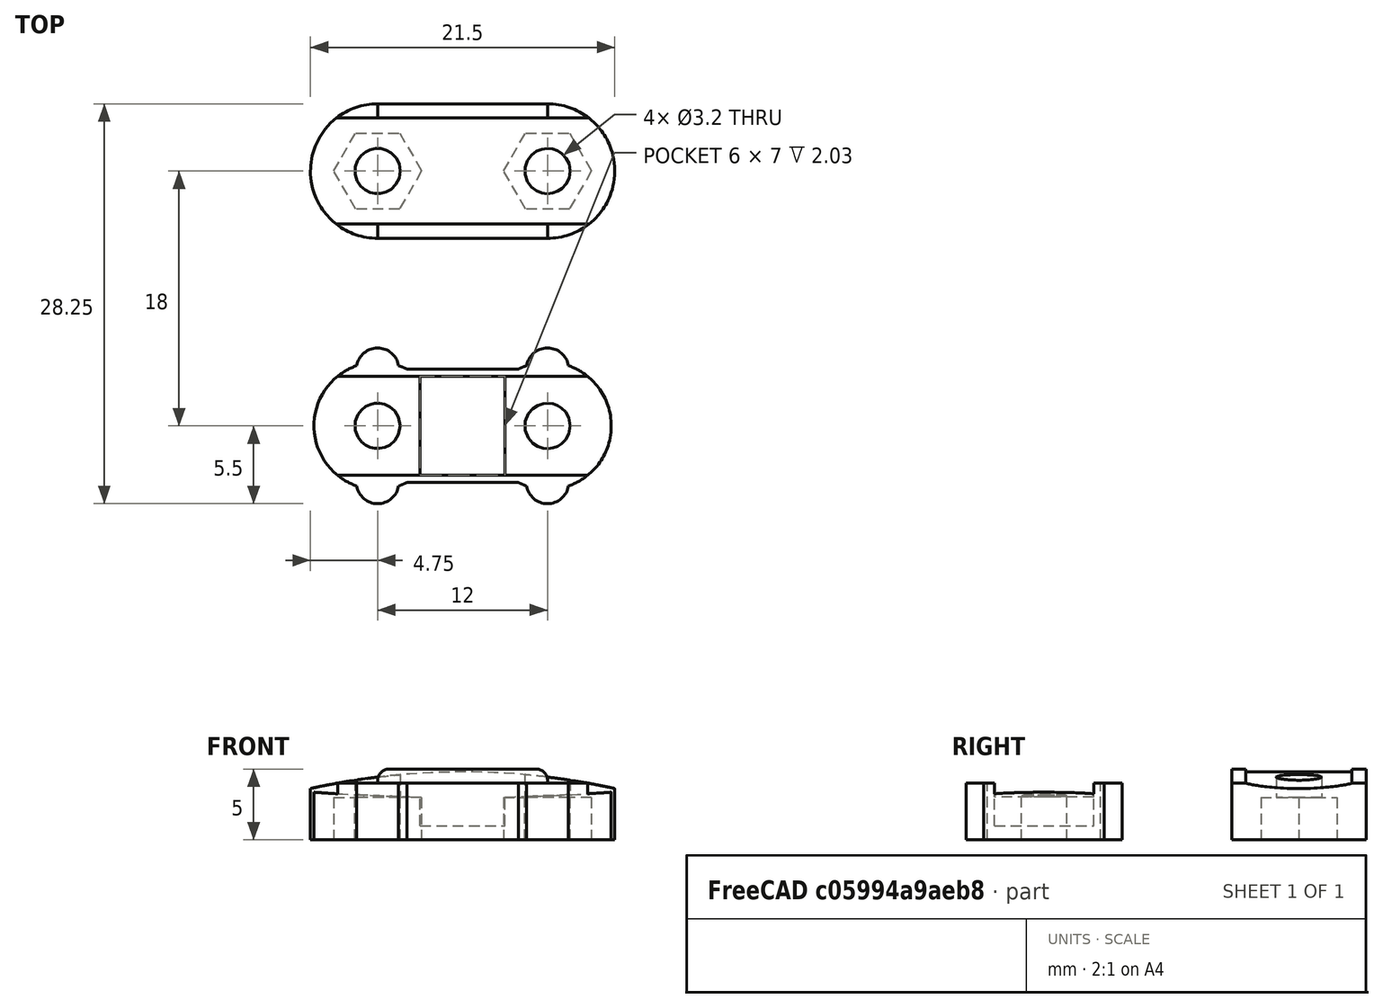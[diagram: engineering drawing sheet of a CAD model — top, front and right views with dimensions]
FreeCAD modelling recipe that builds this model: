
FCSTD DOCUMENT  (FreeCAD 0.16R4864 (Git))
Label: leafspring-mount
License: CC-BY 3.0
LicenseURL: http://creativecommons.org/licenses/by/3.0/
objects: Part::Cylinder×16, Part::Box×14, Part::Cut×12, Part::MultiFuse×10, Part::Extrusion×2, Part::RegularPolygon×1, Part::Feature×1, Part::Fillet×1
note: 57 computed .brp shape members not serialized (recipe doc carries the construction recipe); baked Part::Feature solids carry a one-line shape summary decoded from their .brp

FEATURE [Part::RegularPolygon] RegularPolygon  label="Regular polygon"
  Circumradius = 3.1
  Polygon = 6
FEATURE [Part::Cylinder] Cylinder
  Angle = 360
  Height = 4
  Radius = 4.5
FEATURE [Part::Cylinder] Cylinder001
  Angle = 360
  Height = 4
  Placement = pos=(12,0,0) rot=(0,0,1;0rad)
  Radius = 4.5
FEATURE [Part::Box] Box
  Height = 1
  Length = 12
  Placement = pos=(0,-4,0) rot=(0,0,1;0rad)
  Width = 8
FEATURE [Part::MultiFuse] Fusion
  Shapes = -> [Box,Cylinder001,Cylinder]
FEATURE [Part::Box] Box001
  Height = 4
  Length = 12
  Placement = pos=(0,-4,0) rot=(0,0,1;0rad)
  Width = 1
FEATURE [Part::Box] Box002
  Height = 4
  Length = 12
  Placement = pos=(0,3,0) rot=(0,0,1;0rad)
  Width = 1
FEATURE [Part::Box] Box003
  Height = 1
  Length = 12
  Placement = pos=(0,3.5,3) rot=(0,0,1;0rad)
  Width = 0.5
FEATURE [Part::MultiFuse] Fusion001
  Shapes = -> [Fusion,Box002,Box001]
FEATURE [Part::Box] Box004
  Height = 1
  Length = 12
  Placement = pos=(0,-4,3) rot=(0,0,1;0rad)
  Width = 0.5
FEATURE [Part::MultiFuse] Fusion002
  Shapes = -> [Fusion001,Box003,Box004]
FEATURE [Part::Cylinder] Cylinder002
  Angle = 360
  Height = 4
  Radius = 1.5
FEATURE [Part::Box] Box005
  Height = 10
  Length = 10
  Placement = pos=(-5,0,0) rot=(0,0,1;0rad)
  Width = 10
FEATURE [Part::Cut] Cut
  Base = -> Cylinder002
  Placement = pos=(0,-4,0) rot=(0,0,1;0rad)
  Tool = -> Box005
FEATURE [Part::Cylinder] Cylinder003
  Angle = 360
  Height = 4
  Radius = 1.5
FEATURE [Part::Box] Box006
  Height = 10
  Length = 10
  Placement = pos=(-5,0,0) rot=(0,0,1;0rad)
  Width = 10
FEATURE [Part::Cut] Cut001
  Base = -> Cylinder003
  Placement = pos=(12,-4,0) rot=(0,0,1;0rad)
  Tool = -> Box006
FEATURE [Part::Cylinder] Cylinder004
  Angle = 360
  Height = 4
  Radius = 1.5
FEATURE [Part::Box] Box007
  Height = 10
  Length = 10
  Placement = pos=(-5,0,0) rot=(0,0,1;0rad)
  Width = 10
FEATURE [Part::Cut] Cut002
  Base = -> Cylinder004
  Placement = pos=(0,4,0) rot=(0,0,1;3.14159rad)
  Tool = -> Box007
FEATURE [Part::Cylinder] Cylinder005
  Angle = 360
  Height = 4
  Radius = 1.5
FEATURE [Part::Box] Box008
  Height = 10
  Length = 10
  Placement = pos=(-5,0,0) rot=(0,0,1;0rad)
  Width = 10
FEATURE [Part::Cut] Cut003
  Base = -> Cylinder005
  Placement = pos=(12,4,0) rot=(0,0,1;3.14159rad)
  Tool = -> Box008
FEATURE [Part::MultiFuse] Fusion003
  Shapes = -> [Fusion002,Cut003,Cut002,Cut001,Cut]
FEATURE [Part::Cylinder] Cylinder006
  Angle = 360
  Height = 10
  Radius = 1.6
FEATURE [Part::Cylinder] Cylinder007
  Angle = 360
  Height = 10
  Placement = pos=(12,0,0) rot=(0,0,1;0rad)
  Radius = 1.6
FEATURE [Part::MultiFuse] Fusion004
  Shapes = -> [Cylinder007,Cylinder006]
FEATURE [Part::Cut] Cut004
  Base = -> Fusion003
  Tool = -> Fusion004
FEATURE [Part::Cylinder] Cylinder008
  Angle = 360
  Height = 7
  Placement = pos=(6,3.5,153) rot=(1,0,0;1.5708rad)
  Radius = 150
FEATURE [Part::Cut] Cut005
  Base = -> Cut004
  Tool = -> Cylinder008
FEATURE [Part::Box] Box009
  Height = 3
  Length = 6
  Placement = pos=(3,-3.5,1) rot=(0,0,1;0rad)
  Width = 7
FEATURE [Part::Cut] Cut006
  Base = -> Cut005
  Tool = -> Box009
FEATURE [Part::Feature] Face
  shape: bbox 6.2 x 5.369 x 2e-07 mm, 1 faces, 0 solids (baked)
FEATURE [Part::Extrusion] Extrude
  Base = -> Face
  Dir = (0,0,3)
  Placement = pos=(12,-18,1) rot=(0,0,1;0rad)
  Solid = false
FEATURE [Part::Cylinder] Cylinder009
  Angle = 360
  Height = 4
  Placement = pos=(12,-18,0) rot=(0,0,1;0rad)
  Radius = 4.75
FEATURE [Part::Cylinder] Cylinder010
  Angle = 360
  Height = 4
  Placement = pos=(0,-18,0) rot=(0,0,1;0rad)
  Radius = 4.75
FEATURE [Part::Extrusion] Extrude001
  Base = -> Face
  Dir = (0,0,3)
  Placement = pos=(0,-18,1) rot=(0,0,1;0rad)
  Solid = false
FEATURE [Part::Box] Box010
  Height = 4
  Length = 12
  Placement = pos=(0,-22.75,0) rot=(0,0,1;0rad)
  Width = 9.5
FEATURE [Part::Box] Box011
  Height = 2
  Length = 12
  Placement = pos=(0,-22.75,-1) rot=(0,0,1;0rad)
  Width = 1
FEATURE [Part::Box] Box012
  Height = 2
  Length = 12
  Placement = pos=(0,-14.25,-1) rot=(0,0,1;0rad)
  Width = 1
FEATURE [Part::Cylinder] Cylinder011
  Angle = 360
  Height = 7.5
  Placement = pos=(6,-14.25,49.2) rot=(1,0,0;1.5708rad)
  Radius = 50
FEATURE [Part::Box] Box013
  Height = 300
  Length = 317
  Placement = pos=(-150,-22,0) rot=(0,0,1;0rad)
  Width = 10
FEATURE [Part::Cylinder] Cylinder012
  Angle = 360
  Height = 10
  Placement = pos=(0,-18,-9.2) rot=(0,0,1;0rad)
  Radius = 1.6
FEATURE [Part::Cylinder] Cylinder013
  Angle = 360
  Height = 10
  Placement = pos=(12,-18,-9.2) rot=(0,0,1;0rad)
  Radius = 1.6
FEATURE [Part::MultiFuse] Fusion005
  Placement = pos=(0,0,5) rot=(0,0,1;0rad)
  Shapes = -> [Cylinder013,Cylinder012]
FEATURE [Part::MultiFuse] Fusion006
  Shapes = -> [Box010,Box011,Box012]
FEATURE [Part::Fillet] Fillet
  Base = -> Fusion006
  Edges = 4 edges r=0.8: [Edge1,Edge3,Edge14,Edge15]
FEATURE [Part::MultiFuse] Fusion007
  Shapes = -> [Fillet,Cylinder009,Cylinder010]
FEATURE [Part::Cylinder] Cylinder014
  Angle = 360
  Height = 7.5
  Placement = pos=(6,-14.25,49.2) rot=(1,0,0;1.5708rad)
  Radius = 50
FEATURE [Part::Cylinder] Cylinder015
  Angle = 360
  Height = 7.5
  Placement = pos=(6,-14.25,49.2) rot=(1,0,0;1.5708rad)
  Radius = 51
FEATURE [Part::Cut] Cut007
  Base = -> Cylinder011
  Tool = -> Box013
FEATURE [Part::Cut] Cut008
  Base = -> Cylinder015
  Tool = -> Cylinder014
FEATURE [Part::MultiFuse] Fusion008
  Shapes = -> [Fusion007,Cut007]
FEATURE [Part::Cut] Cut009
  Base = -> Fusion008
  Tool = -> Cut008
FEATURE [Part::MultiFuse] Fusion009
  Shapes = -> [Extrude001,Extrude]
FEATURE [Part::Cut] Cut010
  Base = -> Cut009
  Tool = -> Fusion009
FEATURE [Part::Cut] Cut011
  Base = -> Cut010
  Placement = pos=(0,0,4) rot=(1,0,0;3.14159rad)
  Tool = -> Fusion005
